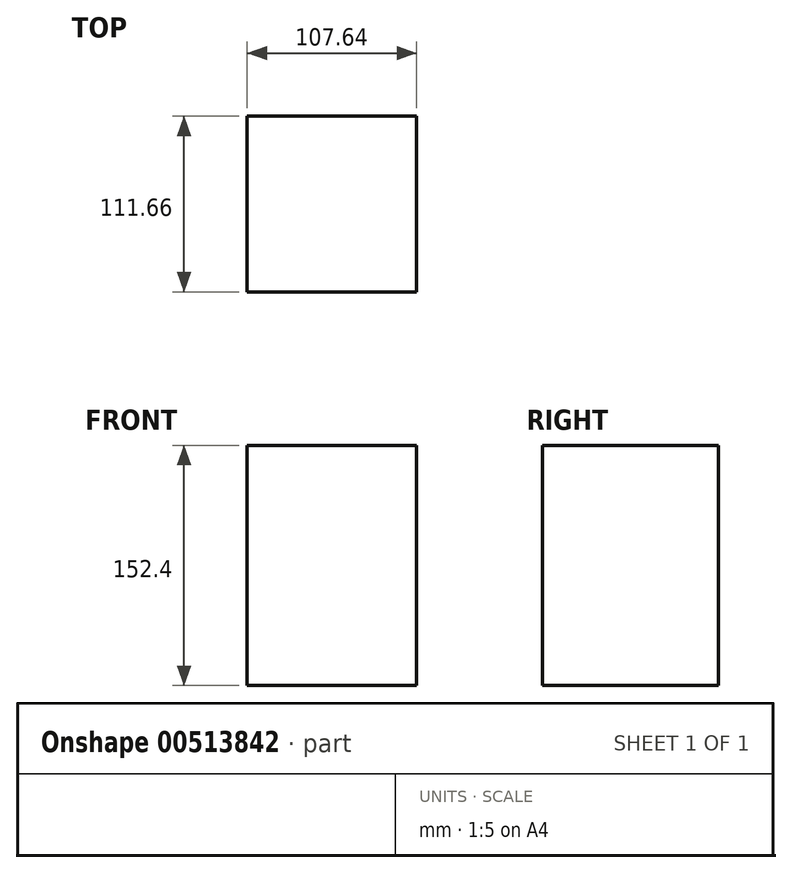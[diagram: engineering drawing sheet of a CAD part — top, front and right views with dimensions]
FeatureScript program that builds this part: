
annotation { "Feature Type Name" : "Feature", "Feature Type Description" : "" }
export const myFeature = defineFeature(function(context is Context, id is Id, definition is map)
    precondition{}
    {
        {
            var Q0;
            Q0=qCreatedBy(makeId("Top.planeOp"),FACE);
            var sketch = newSketch(context, id + "F0", { "sketchPlane" : qUnion([Q0])});
            skLineSegment(sketch, "E0.bottom", {"start": v(53.82, 55.83) * mm, "end": v(-53.82, 55.83) * mm});
            skLineSegment(sketch, "E0.top", {"start": v(53.82, -55.83) * mm, "end": v(-53.82, -55.83) * mm});
            skLineSegment(sketch, "E0.left", {"start": v(53.82, 55.83) * mm, "end": v(53.82, -55.83) * mm});
            skLineSegment(sketch, "E0.right", {"start": v(-53.82, 55.83) * mm, "end": v(-53.82, -55.83) * mm});
            skPoint(sketch, "E0.middle", {"position": v(0, 0) * mm});
            skSolve(sketch);
        }
        {
            var Q0;
            Q0 = qSketchRegion(id + "F0", true);
            extrude(context, id + "F1", {"entities" : qUnion([Q0]), "depth" : 152.4 * mm});
        }
        {
            var Q0;
            Q0=qCreatedBy(makeId("Top.planeOp"),FACE);
            var sketch = newSketch(context, id + "F2", { "sketchPlane" : qUnion([Q0])});
            skCircle(sketch, "E1", {"center": v(0, 0) * mm, "radius": 38.48 * mm});
            skSolve(sketch);
        }
        {
            var Q0;
            Q0 = qSketchRegion(id + "F2", true);
            extrude(context, id + "F3", {"entities" : qUnion([Q0]), "operationType" : NewBodyOperationType.ADD, "oppositeDirection" : true, "depth" : -152.4 * mm});
        }
    });
